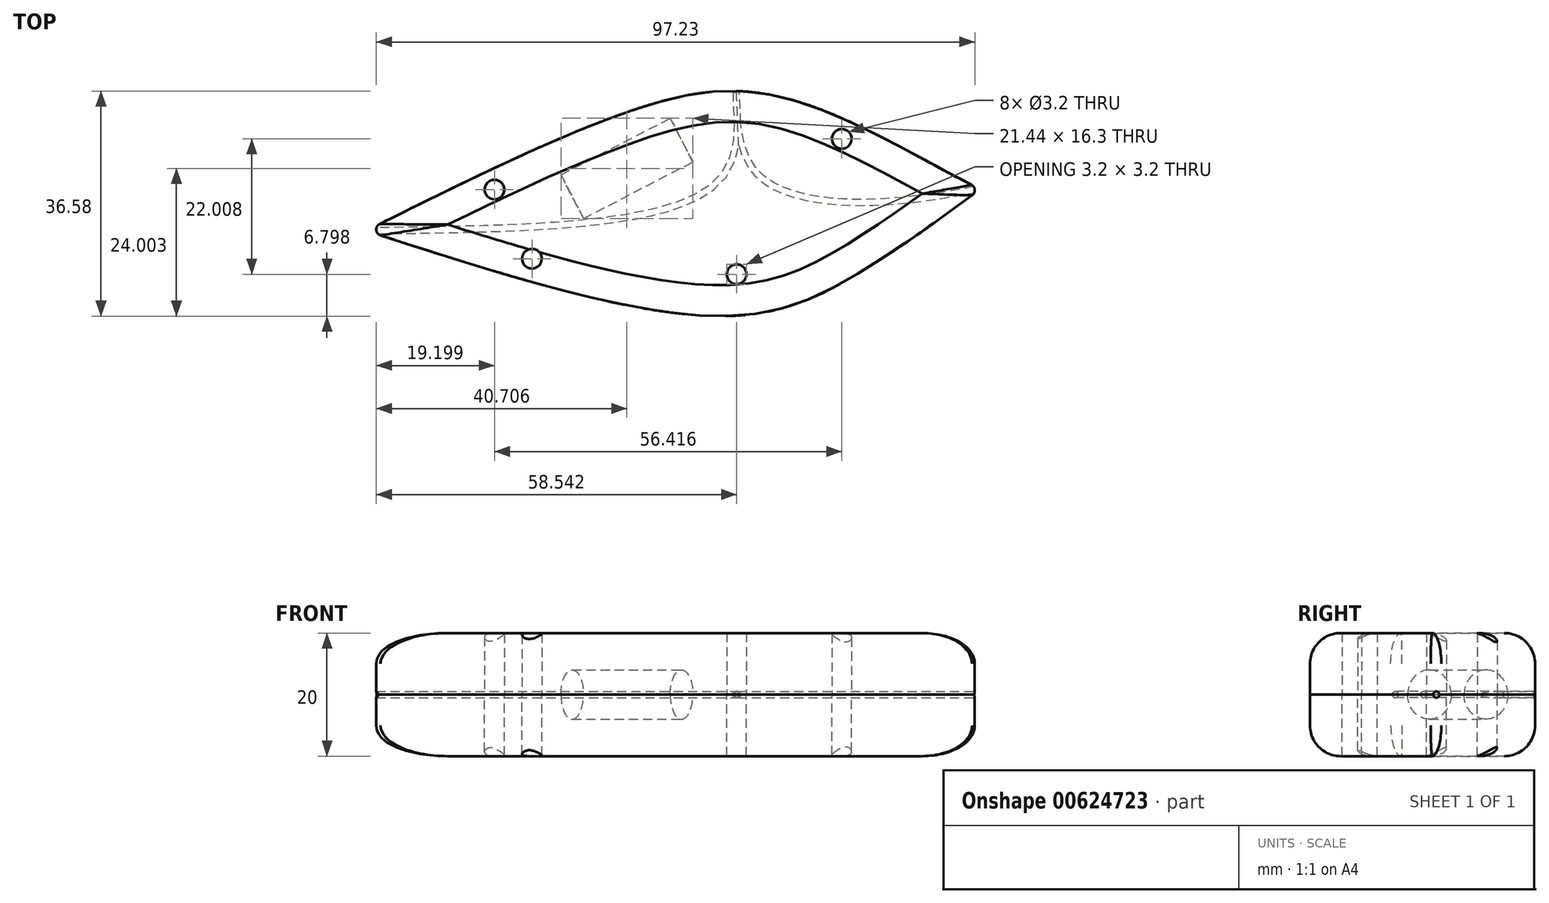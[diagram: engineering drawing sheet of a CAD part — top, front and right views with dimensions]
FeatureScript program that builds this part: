
annotation { "Feature Type Name" : "Feature", "Feature Type Description" : "" }
export const myFeature = defineFeature(function(context is Context, id is Id, definition is map)
    precondition{}
    {
        {
            var Q0;
            Q0=qCreatedBy(makeId("Top.planeOp"),FACE);
            var sketch = newSketch(context, id + "F0", { "sketchPlane" : qUnion([Q0])});
            skFitSpline(sketch, "E0", {"points": [v(0, 20) * mm, v(44.56, 40) * mm, v(73.05, 40) * mm, v(100, 26.9) * mm, v(100, 27.35) * mm], "startDerivative": vector(126.34, 63) * mm, "endDerivative": vector(-5.6, 16.55) * mm});
            skFitSpline(sketch, "E1", {"points": [v(100, 26.9) * mm, v(80.57, 13.45) * mm, v(58.92, 6.15) * mm, v(0, 20) * mm], "startDerivative": vector(-69.83, -51.02) * mm, "endDerivative": vector(-148.42, 47.98) * mm});
            skSolve(sketch);
        }
        {
            var Q0;
            {var subQ0=sQuery(id+"F0.wireOp",EDGE,"E1");Q0=makeQuery(id+"F0.imprint","IMPRINT",FACE,{"disambiguationData":[TD([[makeQuery(id+"F0.imprint","IMPRINT",EDGE,{"derivedFrom":subQ0}),-1.0]])]});}
            extrude(context, id + "F1", {"entities" : qUnion([Q0]), "depth" : 10 * mm, "offsetDistance" : 25 * mm});
        }
        {
            var Q0;
            Q0=makeQuery(id+"F1.opExtrude","CAP_FACE",FACE,{"disambiguationData":[OSD([sQuery(id+"F0.wireOp",EDGE,"E0"),sQuery(id+"F0.wireOp",EDGE,"E1")])],"isStart":false});
            fillet(context, id + "F2", {"entities" : qUnion([Q0]), "radius" : 5 * mm, "tangentPropagation" : true, "allowEdgeOverflow" : false});
        }
        {
            var Q0;
            {var subQ0=sQuery(id+"F0.wireOp",EDGE,"E1");var subQ1=sQuery(id+"F0.wireOp",EDGE,"E0");Q0=makeQuery(id+"F1.opExtrude","SWEPT_EDGE",EDGE,{"disambiguationData":[OSD([subQ1,subQ0]),TDD([makeQuery(id+"F0.imprint","INTERSECT",VERTEX,{"disambiguationData":[OD(1.0)],"derivedFrom":[subQ1,subQ0]})])]});}
            cPlane(context, id + "F3", {"entities" : qUnion([Q0]), "cplaneType" : CPlaneType.LINE_ANGLE, "offset" : 25 * mm, "angle" : 0 * degree, "width" : 150 * mm, "height" : 150 * mm});
        }
        {
            var Q0;
            Q0=qCreatedBy(id+"F3.planeOp",FACE);
            var sketch = newSketch(context, id + "F4", { "sketchPlane" : qUnion([Q0])});
            skCircle(sketch, "E2", {"center": v(-26.9, 0) * mm, "radius": 0.5 * mm});
            skSolve(sketch);
        }
        {
            var Q0;
            Q0=makeQuery(id+"F1.opExtrude","CAP_FACE",FACE,{"disambiguationData":[OSD([sQuery(id+"F0.wireOp",EDGE,"E0"),sQuery(id+"F0.wireOp",EDGE,"E1")])],"isStart":true});
            var sketch = newSketch(context, id + "F5", { "sketchPlane" : qUnion([Q0])});
            skFitSpline(sketch, "E3", {"points": [v(100, -26.9) * mm, v(80.67, -24.6) * mm, v(63.64, -29.1) * mm, v(60.08, -42.7) * mm], "startDerivative": vector(-52.27, 9.52) * mm, "endDerivative": vector(-0.42, -51.65) * mm});
            skFitSpline(sketch, "E4", {"points": [v(59.95, -44.22) * mm, v(57.18, -28.02) * mm, v(0, -20) * mm], "startDerivative": vector(2.9, 48.67) * mm, "endDerivative": vector(-111.64, 1.76) * mm});
            skSolve(sketch);
        }
        {
            var Q0;
            Q0=makeQuery(id+"F4.imprint","IMPRINT",FACE,{"disambiguationData":[TD([[makeQuery(id+"F4.imprint","IMPRINT",EDGE,{"derivedFrom":sQuery(id+"F4.wireOp",EDGE,"E2")}),1.0]])]});
            var Q1;
            Q1=sQuery(id+"F5.wireOp",EDGE,"E3");
            sweep(context, id + "F6", {"operationType" : NewBodyOperationType.REMOVE, "profiles" : qUnion([Q0]), "path" : qUnion([Q1])});
        }
        {
            var Q0;
            Q0=makeQuery(id+"F6.boolean.opBoolean","INTERSECT",EDGE,{"derivedFrom":[makeQuery(id+"F1.opExtrude","SWEPT_FACE",FACE,{"disambiguationData":[OSD([sQuery(id+"F0.wireOp",EDGE,"E0")])]}),makeQuery(id+"F6.opSweep","CAP_FACE",FACE,{"disambiguationData":[OSD([sQuery(id+"F4.wireOp",EDGE,"E2"),sQuery(id+"F5.wireOp",VERTEX,"E3.end")])],"isStart":false})]});
            cPlane(context, id + "F7", {"entities" : qUnion([Q0]), "cplaneType" : CPlaneType.LINE_ANGLE, "offset" : 25 * mm, "angle" : 90 * degree, "width" : 150 * mm, "height" : 150 * mm});
        }
        {
            var Q0;
            Q0=qCreatedBy(id+"F7.planeOp",FACE);
            var sketch = newSketch(context, id + "F8", { "sketchPlane" : qUnion([Q0])});
            skCircle(sketch, "E5", {"center": v(-60.08, 0) * mm, "radius": 0.5 * mm});
            skSolve(sketch);
        }
        {
            var Q0;
            Q0=makeQuery(id+"F8.imprint","IMPRINT",FACE,{"disambiguationData":[TD([[makeQuery(id+"F8.imprint","IMPRINT",EDGE,{"derivedFrom":sQuery(id+"F8.wireOp",EDGE,"E5")}),1.0]])]});
            extrude(context, id + "F9", {"entities" : qUnion([Q0]), "operationType" : NewBodyOperationType.REMOVE, "oppositeDirection" : true, "depth" : 0.2 * mm, "offsetDistance" : 25 * mm});
        }
        {
            var Q0;
            Q0=makeQuery(id+"F8.imprint","IMPRINT",FACE,{"disambiguationData":[TD([[makeQuery(id+"F8.imprint","IMPRINT",EDGE,{"derivedFrom":sQuery(id+"F8.wireOp",EDGE,"E5")}),1.0]])]});
            var Q1;
            Q1=sQuery(id+"F8.wireOp",EDGE,"E5");
            var Q2;
            Q2=sQuery(id+"F5.wireOp",EDGE,"E4");
            sweep(context, id + "F10", {"operationType" : NewBodyOperationType.REMOVE, "profiles" : qUnion([Q0]), "surfaceProfiles" : qUnion([Q1]), "path" : qUnion([Q2])});
        }
        {
            var Q0;
            {var subQ0=sQuery(id+"F0.wireOp",EDGE,"E1");var subQ1=sQuery(id+"F0.wireOp",EDGE,"E0");Q0=makeQuery(id+"F1.opExtrude","SWEPT_EDGE",EDGE,{"disambiguationData":[OSD([subQ1,subQ0]),TDD([makeQuery(id+"F0.imprint","INTERSECT",VERTEX,{"disambiguationData":[OD(0.0)],"derivedFrom":[subQ1,subQ0]})])]});}
            fillet(context, id + "F11", {"entities" : qUnion([Q0]), "radius" : 1 * mm, "tangentPropagation" : true, "allowEdgeOverflow" : false});
        }
        {
            var Q0;
            {var subQ0=sQuery(id+"F0.wireOp",EDGE,"E1");var subQ1=sQuery(id+"F0.wireOp",EDGE,"E0");Q0=makeQuery(id+"F1.opExtrude","SWEPT_EDGE",EDGE,{"disambiguationData":[OSD([subQ1,subQ0]),TDD([makeQuery(id+"F0.imprint","INTERSECT",VERTEX,{"disambiguationData":[OD(1.0)],"derivedFrom":[subQ1,subQ0]})])]});}
            fillet(context, id + "F12", {"entities" : qUnion([Q0]), "radius" : 1 * mm, "tangentPropagation" : true, "allowEdgeOverflow" : false});
        }
        {
            var Q0;
            {var subQ5=makeQuery(id+"F1.opExtrude","CAP_EDGE",EDGE,{"disambiguationData":[OSD([sQuery(id+"F0.wireOp",EDGE,"E1")])],"isStart":true});Q0=makeQuery(id+"F5.imprint","IMPRINT",FACE,{"disambiguationData":[TD([[makeQuery(id+"F5.imprint","IMPRINT",EDGE,{"derivedFrom":subQ5}),1.0]])]});}
            var sketch = newSketch(context, id + "F13", { "sketchPlane" : qUnion([Q0])});
            skLineSegment(sketch, "E6", {"start": v(55.4, -26.67) * mm, "end": v(48.07, -40.81) * mm});
            skSolve(sketch);
        }
        {
            var Q0;
            Q0=sQuery(id+"F13.wireOp",EDGE,"E6");
            cPlane(context, id + "F14", {"entities" : qUnion([Q0]), "cplaneType" : CPlaneType.LINE_ANGLE, "offset" : 25 * mm, "angle" : 90 * degree, "width" : 150 * mm, "height" : 150 * mm});
        }
        {
            var Q0;
            Q0=qCreatedBy(id+"F14.planeOp",FACE);
            var sketch = newSketch(context, id + "F15", { "sketchPlane" : qUnion([Q0])});
            skCircle(sketch, "E7", {"center": v(7.28, 0) * mm, "radius": 4 * mm});
            skSolve(sketch);
        }
        {
            var Q0;
            Q0=makeQuery(id+"F15.imprint","IMPRINT",FACE,{"disambiguationData":[TD([[makeQuery(id+"F15.imprint","IMPRINT",EDGE,{"derivedFrom":sQuery(id+"F15.wireOp",EDGE,"E7")}),1.0]])]});
            extrude(context, id + "F16", {"entities" : qUnion([Q0]), "operationType" : NewBodyOperationType.REMOVE, "oppositeDirection" : true, "depth" : 20 * mm, "offsetDistance" : 25 * mm});
        }
        {
            var Q0;
            {var subQ5=makeQuery(id+"F1.opExtrude","CAP_EDGE",EDGE,{"disambiguationData":[OSD([sQuery(id+"F0.wireOp",EDGE,"E1")])],"isStart":true});Q0=makeQuery(id+"F5.imprint","IMPRINT",FACE,{"disambiguationData":[TD([[makeQuery(id+"F5.imprint","IMPRINT",EDGE,{"derivedFrom":subQ5}),1.0]])]});}
            var sketch = newSketch(context, id + "F17", { "sketchPlane" : qUnion([Q0])});
            skCircle(sketch, "E8", {"center": v(60.18, -12.93) * mm, "radius": 1.6 * mm});
            skCircle(sketch, "E9", {"center": v(20.84, -26.69) * mm, "radius": 1.6 * mm});
            skCircle(sketch, "E10", {"center": v(26.92, -15.46) * mm, "radius": 1.6 * mm});
            skCircle(sketch, "E11", {"center": v(77.26, -34.94) * mm, "radius": 1.6 * mm});
            skSolve(sketch);
        }
        {
            var Q0;
            Q0 = qSketchRegion(id + "F17", true);
            extrude(context, id + "F18", {"entities" : qUnion([Q0]), "operationType" : NewBodyOperationType.REMOVE, "oppositeDirection" : true, "depth" : 25 * mm, "offsetDistance" : 25 * mm});
        }
        {
            var Q0;
            Q0=makeQuery(id+"F1.opExtrude","SWEPT_BODY",BODY,{"disambiguationData":[OSD([sQuery(id+"F0.wireOp",EDGE,"E0"),sQuery(id+"F0.wireOp",EDGE,"E1")])]});
            var Q1;
            Q1=qCreatedBy(makeId("Top.planeOp"),FACE);
            mirror(context, id + "F19", {"entities" : qUnion([Q0]), "mirrorPlane" : qUnion([Q1])});
        }
    });
